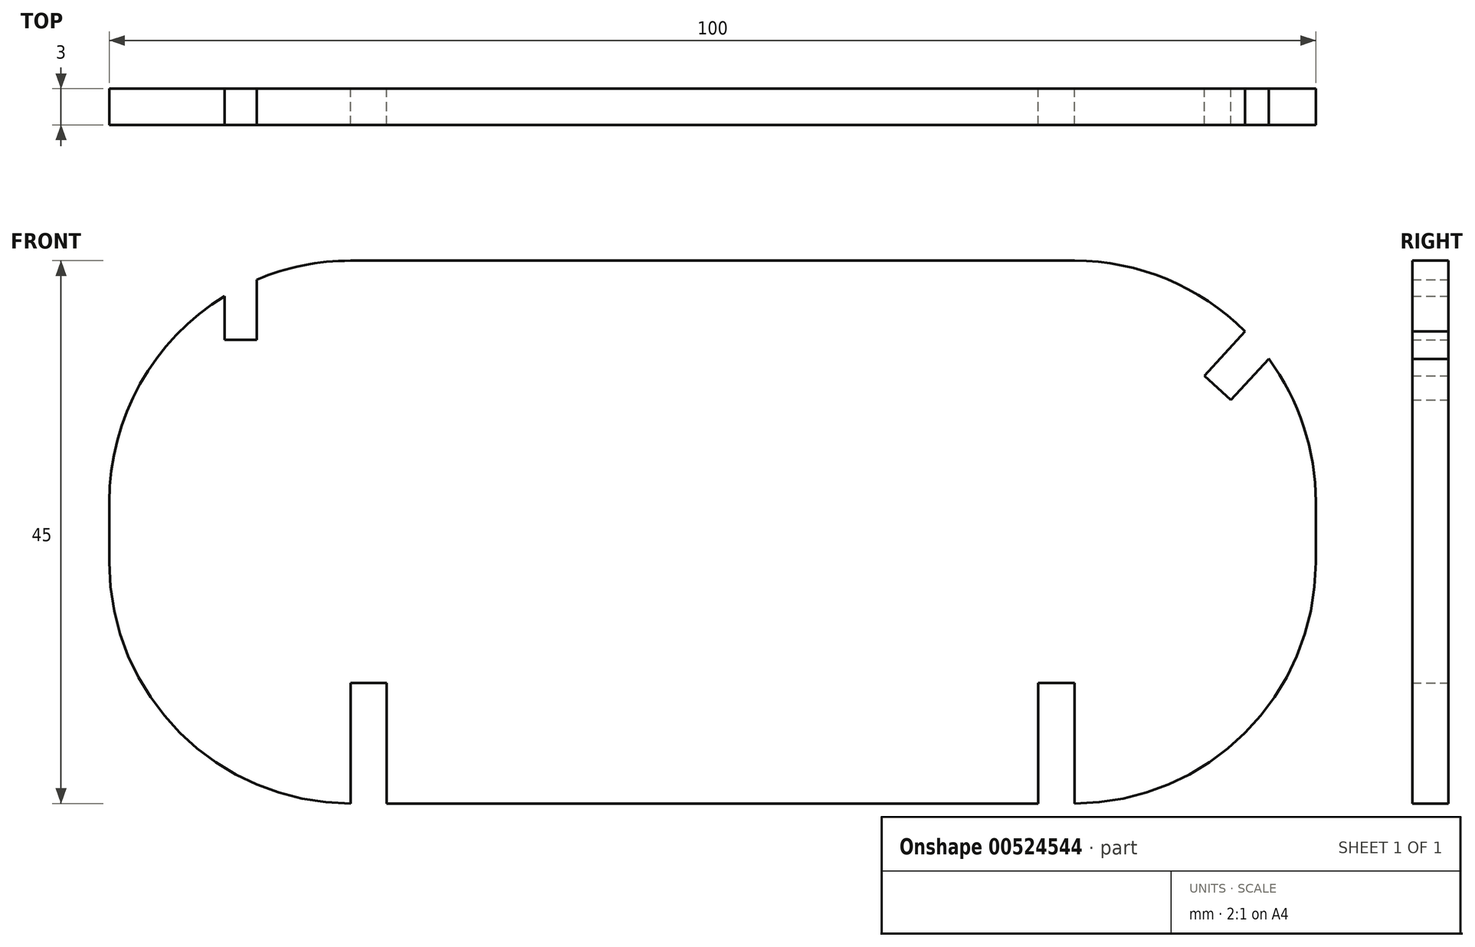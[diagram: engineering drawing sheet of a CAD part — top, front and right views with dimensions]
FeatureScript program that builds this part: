
annotation { "Feature Type Name" : "Feature", "Feature Type Description" : "" }
export const myFeature = defineFeature(function(context is Context, id is Id, definition is map)
    precondition{}
    {
        {
            var Q0;
            Q0=qCreatedBy(makeId("Front.planeOp"),FACE);
            var sketch = newSketch(context, id + "F0", { "sketchPlane" : qUnion([Q0])});
            skLineSegment(sketch, "E0", {"start": v(-32.32, 25.98) * mm, "end": v(27.68, 25.98) * mm});
            skLineSegment(sketch, "E1", {"start": v(-52.32, 5.98) * mm, "end": v(-52.32, 0.98) * mm});
            skLineSegment(sketch, "E2", {"start": v(-29.32, -19.02) * mm, "end": v(24.68, -19.02) * mm});
            skLineSegment(sketch, "E3", {"start": v(47.68, 0.98) * mm, "end": v(47.68, 5.98) * mm});
            skPoint(sketch, "E4.visualSharp", {"position": v(-52.32, 25.98) * mm});
            skArc(sketch, "E4.filletArc", {"start": v(-32.32, 25.98) * mm, "mid": v(-36.3, 25.58) * mm, "end": v(-40.1, 24.4) * mm});
            skPoint(sketch, "E5.visualSharp", {"position": v(-52.32, -19.02) * mm});
            skArc(sketch, "E5.filletArc", {"start": v(-52.32, 0.98) * mm, "mid": v(-46.47, -13.16) * mm, "end": v(-32.32, -19.02) * mm});
            skPoint(sketch, "E6.visualSharp", {"position": v(47.68, 25.98) * mm});
            skArc(sketch, "E6.filletArc", {"start": v(47.68, 5.98) * mm, "mid": v(46.67, 12.22) * mm, "end": v(43.77, 17.85) * mm});
            skPoint(sketch, "E7.visualSharp", {"position": v(47.68, -19.02) * mm});
            skArc(sketch, "E7.filletArc", {"start": v(27.68, -19.02) * mm, "mid": v(41.82, -13.16) * mm, "end": v(47.68, 0.98) * mm});
            skLineSegment(sketch, "E8", {"start": v(-32.32, -19.02) * mm, "end": v(-32.32, -9.02) * mm});
            skLineSegment(sketch, "E9", {"start": v(-32.32, -9.02) * mm, "end": v(-29.32, -9.02) * mm});
            skLineSegment(sketch, "E10", {"start": v(-29.32, -9.02) * mm, "end": v(-29.32, -19.02) * mm});
            skLineSegment(sketch, "E11", {"start": v(27.68, -19.02) * mm, "end": v(27.68, -9.02) * mm});
            skLineSegment(sketch, "E12", {"start": v(27.68, -9.02) * mm, "end": v(24.68, -9.02) * mm});
            skLineSegment(sketch, "E13", {"start": v(24.68, -9.02) * mm, "end": v(24.68, -19.02) * mm});
            skLineSegment(sketch, "E14", {"start": v(-42.77, 23.03) * mm, "end": v(-42.77, 19.4) * mm});
            skLineSegment(sketch, "E15", {"start": v(-42.77, 19.4) * mm, "end": v(-40.1, 19.4) * mm});
            skLineSegment(sketch, "E16", {"start": v(-40.1, 19.4) * mm, "end": v(-40.1, 24.4) * mm});
            skArc(sketch, "E17.trimOffspring", {"start": v(-42.77, 23.03) * mm, "mid": v(-49.77, 15.75) * mm, "end": v(-52.32, 5.98) * mm});
            skLineSegment(sketch, "E18", {"start": v(41.82, 20.12) * mm, "end": v(38.44, 16.44) * mm});
            skLineSegment(sketch, "E19", {"start": v(38.44, 16.44) * mm, "end": v(40.63, 14.42) * mm});
            skLineSegment(sketch, "E20", {"start": v(40.63, 14.42) * mm, "end": v(43.77, 17.85) * mm});
            skArc(sketch, "E21.trimOffspring", {"start": v(41.82, 20.12) * mm, "mid": v(35.33, 24.46) * mm, "end": v(27.68, 25.98) * mm});
            skSolve(sketch);
        }
        {
            var Q0;
            Q0=makeQuery(id+"F0.imprint","IMPRINT",FACE,{"disambiguationData":[TD([[makeQuery(id+"F0.imprint","IMPRINT",EDGE,{"derivedFrom":sQuery(id+"F0.wireOp",EDGE,"E0")}),-1.0]])]});
            extrude(context, id + "F1", {"entities" : qUnion([Q0]), "depth" : 3 * mm, "offsetDistance" : 25 * mm});
        }
    });
